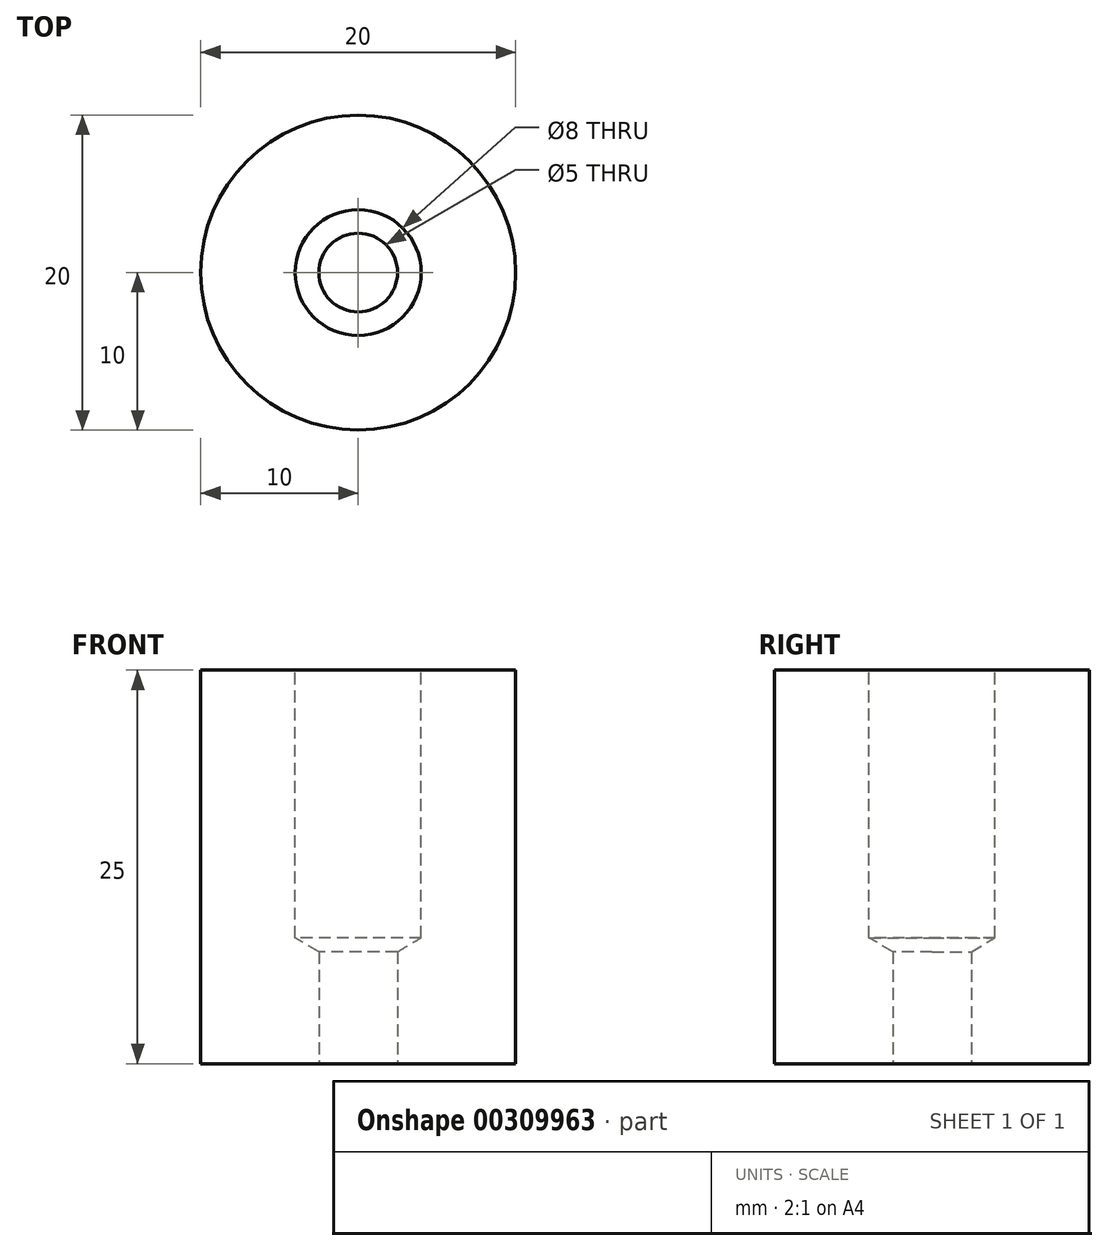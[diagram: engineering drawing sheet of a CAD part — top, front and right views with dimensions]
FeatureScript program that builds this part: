
annotation { "Feature Type Name" : "Feature", "Feature Type Description" : "" }
export const myFeature = defineFeature(function(context is Context, id is Id, definition is map)
    precondition{}
    {
        {
            var Q0;
            Q0=qCreatedBy(makeId("Front.planeOp"),FACE);
            var sketch = newSketch(context, id + "F0", { "sketchPlane" : qUnion([Q0])});
            skLineSegment(sketch, "E0.bottom", {"start": v(-10, 25) * mm, "end": v(0, 25) * mm});
            skLineSegment(sketch, "E0.top", {"start": v(-10, 0) * mm, "end": v(0, 0) * mm});
            skLineSegment(sketch, "E0.left", {"start": v(-10, 25) * mm, "end": v(-10, 0) * mm});
            skLineSegment(sketch, "E0.right", {"start": v(0, 25) * mm, "end": v(0, 0) * mm});
            skSolve(sketch);
        }
        {
            var Q0;
            Q0 = qSketchRegion(id + "F0", true);
            var Q1;
            Q1=sQuery(id+"F0.wireOp",EDGE,"E0.right");
            revolve(context, id + "F1", {"entities" : qUnion([Q0]), "axis" : qUnion([Q1]), "revolveType" : RevolveType.FULL});
        }
        {
            var Q0;
            Q0=makeQuery(id+"F1.opRevolve","SWEPT_FACE",FACE,{"disambiguationData":[OSD([sQuery(id+"F0.wireOp",EDGE,"E0.bottom")])]});
            var sketch = newSketch(context, id + "F2", { "sketchPlane" : qUnion([Q0])});
            skPoint(sketch, "E1", {"position": v(0, 0) * mm});
            skSolve(sketch);
        }
        {
            var Q0;
            Q0=sQuery(id+"F2.wireOp",VERTEX,"E1");
            var Q1;
            Q1=makeQuery(id+"F1.opRevolve","SWEPT_BODY",BODY,{"disambiguationData":[OSD([sQuery(id+"F0.wireOp",EDGE,"E0.bottom"),sQuery(id+"F0.wireOp",EDGE,"E0.top"),sQuery(id+"F0.wireOp",EDGE,"E0.left"),sQuery(id+"F0.wireOp",EDGE,"E0.right")])]});
            hole(context, id + "F3", {"style" : HoleStyle.SIMPLE, "endStyle" : HoleEndStyle.BLIND, "holeDiameter" : 8 * mm, "holeDepth" : 17 * mm, "tappedDepth" : 12 * mm, "tapClearance" : 3, "locations" : qUnion([Q0]), "scope" : qUnion([Q1])});
        }
        {
            var Q0;
            Q0=makeQuery(id+"F1.opRevolve","SWEPT_FACE",FACE,{"disambiguationData":[OSD([sQuery(id+"F0.wireOp",EDGE,"E0.top")])]});
            var sketch = newSketch(context, id + "F4", { "sketchPlane" : qUnion([Q0])});
            skPoint(sketch, "E2", {"position": v(0, 0) * mm});
            skSolve(sketch);
        }
        {
            var Q0;
            Q0=sQuery(id+"F4.wireOp",VERTEX,"E2");
            var Q1;
            Q1=makeQuery(id+"F1.opRevolve","SWEPT_BODY",BODY,{"disambiguationData":[OSD([sQuery(id+"F0.wireOp",EDGE,"E0.bottom"),sQuery(id+"F0.wireOp",EDGE,"E0.top"),sQuery(id+"F0.wireOp",EDGE,"E0.left"),sQuery(id+"F0.wireOp",EDGE,"E0.right")])]});
            hole(context, id + "F5", {"style" : HoleStyle.SIMPLE, "endStyle" : HoleEndStyle.THROUGH, "holeDiameter" : 5 * mm, "tappedDepth" : 12 * mm, "tapClearance" : 3, "locations" : qUnion([Q0]), "scope" : qUnion([Q1])});
        }
    });
